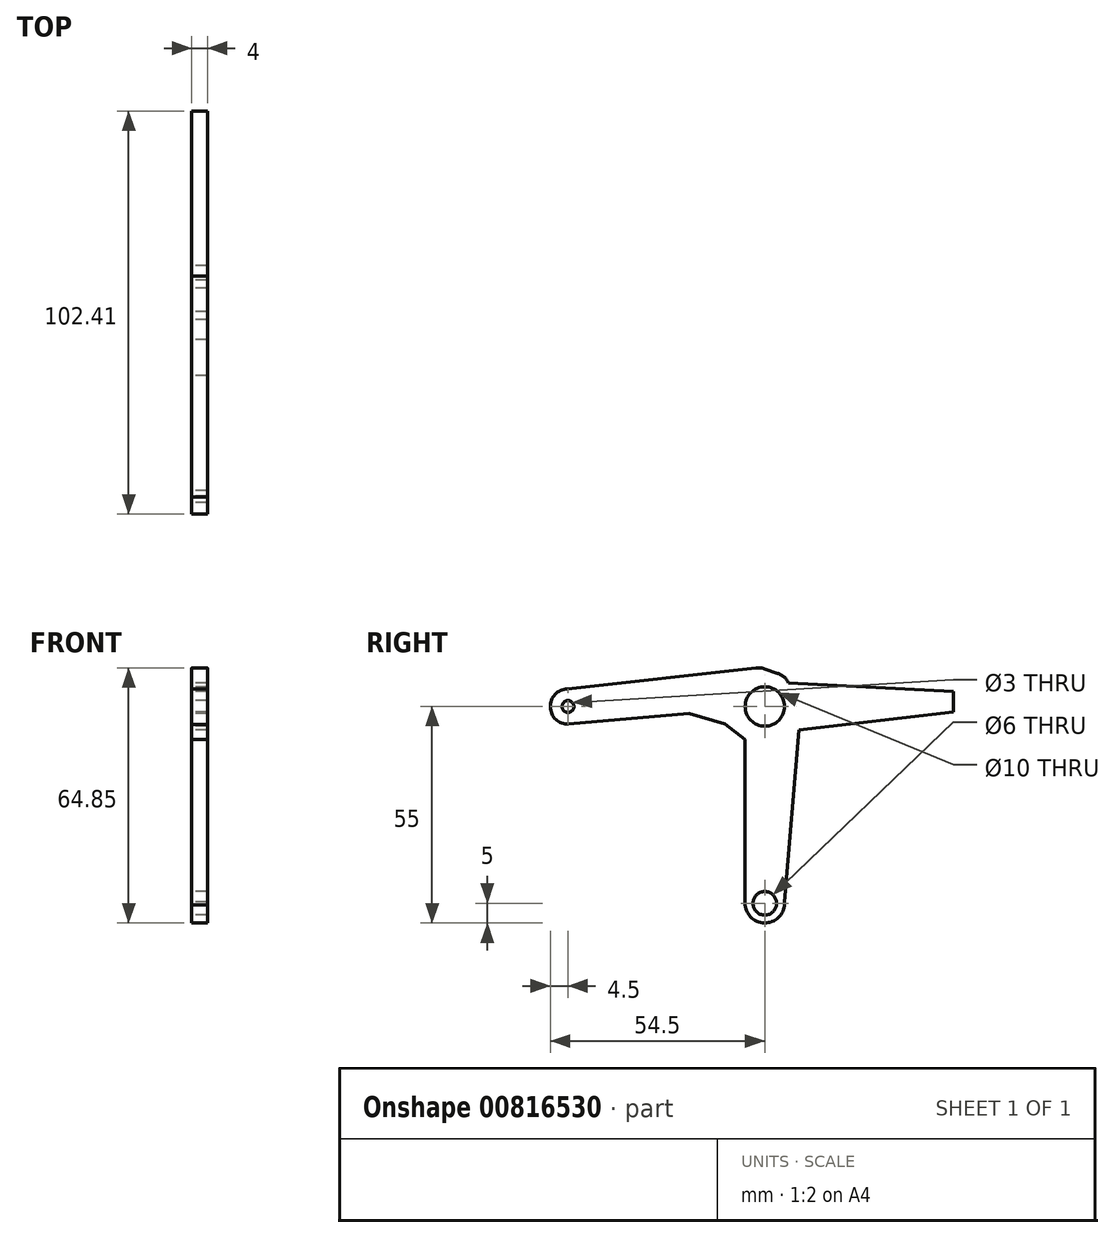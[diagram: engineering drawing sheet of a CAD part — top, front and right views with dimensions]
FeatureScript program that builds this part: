
annotation { "Feature Type Name" : "Feature", "Feature Type Description" : "" }
export const myFeature = defineFeature(function(context is Context, id is Id, definition is map)
    precondition{}
    {
        {
            var Q0;
            Q0=qCreatedBy(makeId("Right.planeOp"),FACE);
            var sketch = newSketch(context, id + "F0", { "sketchPlane" : qUnion([Q0])});
            skCircle(sketch, "E0", {"center": v(0, 0) * mm, "radius": 5 * mm});
            skCircle(sketch, "E1", {"center": v(-50, 0) * mm, "radius": 1.5 * mm});
            skCircle(sketch, "E2", {"center": v(0, -50) * mm, "radius": 3 * mm});
            skArc(sketch, "E3", {"start": v(-50.17, 4.5) * mm, "mid": v(-54.5, -0.16) * mm, "end": v(-49.85, -4.5) * mm});
            skArc(sketch, "E4", {"start": v(-4.98, -50.41) * mm, "mid": v(0.38, -54.99) * mm, "end": v(4.99, -49.65) * mm});
            skLineSegment(sketch, "E5", {"start": v(-50.17, 4.5) * mm, "end": v(-2.21, 9.82) * mm});
            skLineSegment(sketch, "E6", {"start": v(4.86, -51.18) * mm, "end": v(9.07, -1.44) * mm});
            skLineSegment(sketch, "E7", {"start": v(-4.98, -50.41) * mm, "end": v(-4.98, -8.35) * mm});
            skLineSegment(sketch, "E8", {"start": v(-49.85, -4.5) * mm, "end": v(-19.23, -1.78) * mm});
            skLineSegment(sketch, "E9", {"start": v(-19.23, -1.78) * mm, "end": v(-10.07, -4.5) * mm});
            skLineSegment(sketch, "E10", {"start": v(-0.04, 9.58) * mm, "end": v(3.24, 8.45) * mm});
            skLineSegment(sketch, "E11", {"start": v(6.06, 6.03) * mm, "end": v(8.52, 1.28) * mm});
            skPoint(sketch, "E12.visualSharp", {"position": v(-1.1, 9.94) * mm});
            skArc(sketch, "E12.filletArc", {"start": v(-0.04, 9.58) * mm, "mid": v(-1.12, 9.82) * mm, "end": v(-2.21, 9.82) * mm});
            skPoint(sketch, "E13.visualSharp", {"position": v(5.13, 7.8) * mm});
            skArc(sketch, "E13.filletArc", {"start": v(6.06, 6.03) * mm, "mid": v(4.88, 7.51) * mm, "end": v(3.24, 8.45) * mm});
            skPoint(sketch, "E14.visualSharp", {"position": v(9.19, 0) * mm});
            skArc(sketch, "E14.filletArc", {"start": v(9.07, -1.44) * mm, "mid": v(8.99, -0.04) * mm, "end": v(8.52, 1.28) * mm});
            skLineSegment(sketch, "E15", {"start": v(-4.98, -8.35) * mm, "end": v(-10.07, -4.5) * mm});
            skLineSegment(sketch, "E16", {"start": v(6.06, 6.03) * mm, "end": v(47.9, 3.88) * mm});
            skLineSegment(sketch, "E17", {"start": v(47.9, 3.88) * mm, "end": v(47.9, -1.36) * mm});
            skLineSegment(sketch, "E18", {"start": v(47.9, -1.36) * mm, "end": v(8.68, -6.01) * mm});
            skSolve(sketch);
        }
        {
            var Q0;
            Q0=qSketchRegion(id+"F0",true);
            extrude(context, id + "F1", {"entities" : qUnion([Q0]), "depth" : 4 * mm, "offsetDistance" : 25 * mm});
        }
    });
